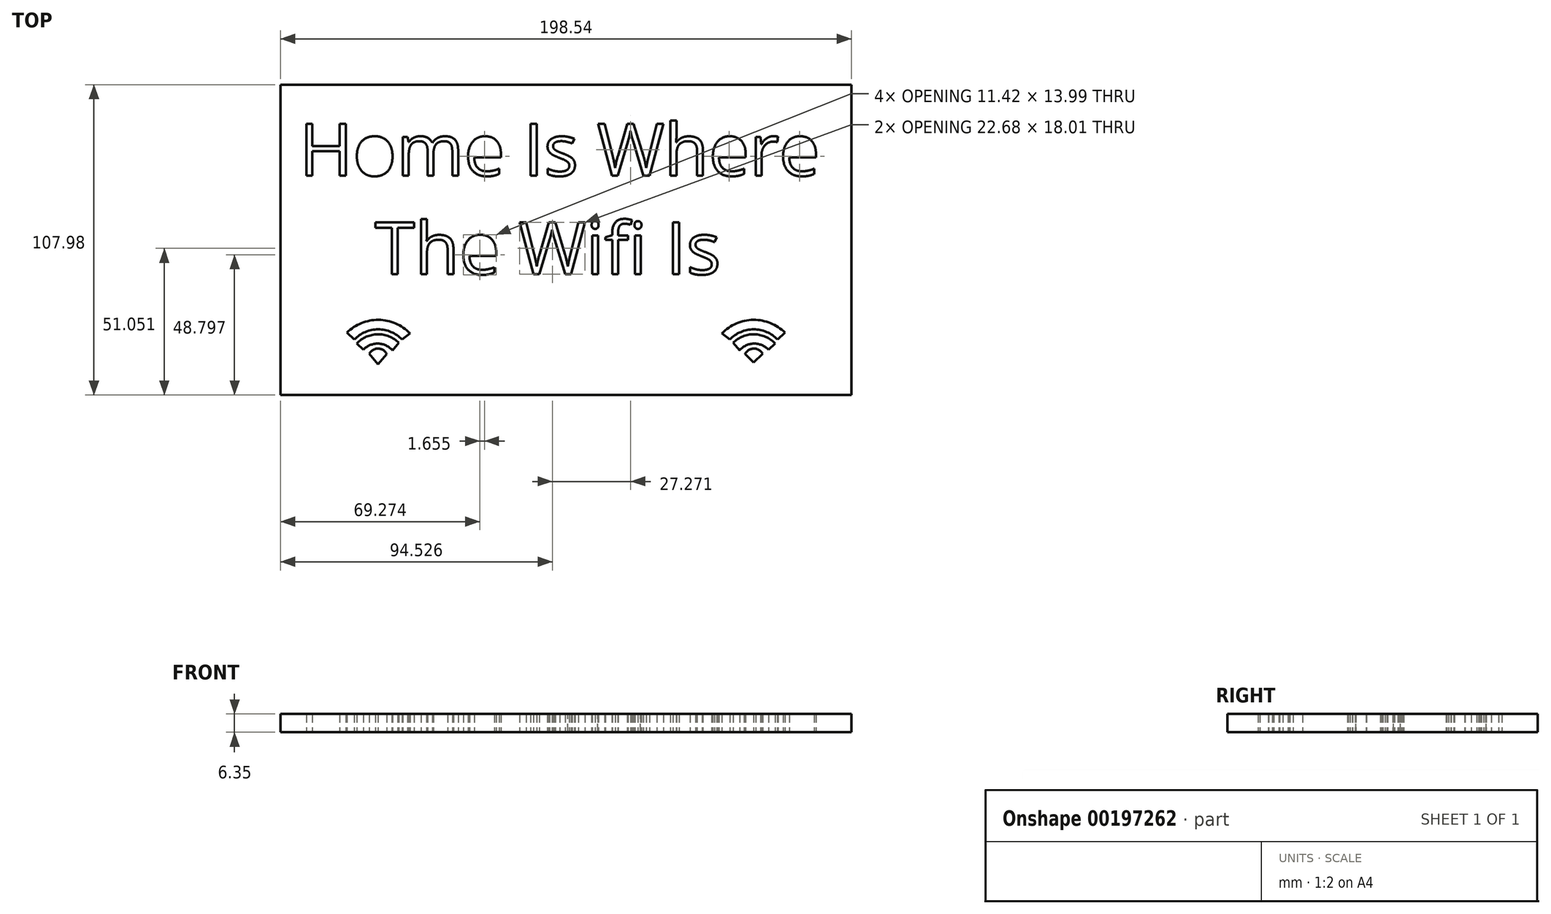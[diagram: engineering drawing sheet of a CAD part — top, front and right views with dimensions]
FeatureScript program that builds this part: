
annotation { "Feature Type Name" : "Feature", "Feature Type Description" : "" }
export const myFeature = defineFeature(function(context is Context, id is Id, definition is map)
    precondition{}
    {
        {
            var Q0;
            Q0=qCreatedBy(makeId("Top.planeOp"),FACE);
            var sketch = newSketch(context, id + "F0", { "sketchPlane" : qUnion([Q0])});
            skText(sketch, "E0", { "text": "Home Is Where \n    The Wifi Is", "fontName": "OpenSans-Regular.ttf"});
            skPoint(sketch, "E1.middle", {"position": v(-127.1, 81.3) * mm});
            skLineSegment(sketch, "E2.bottom", {"start": v(99.27, -53.99) * mm, "end": v(-99.27, -53.99) * mm});
            skLineSegment(sketch, "E2.top", {"start": v(99.27, 53.99) * mm, "end": v(-99.27, 53.99) * mm});
            skLineSegment(sketch, "E2.left", {"start": v(99.27, -53.99) * mm, "end": v(99.27, 53.99) * mm});
            skLineSegment(sketch, "E2.right", {"start": v(-99.27, -53.99) * mm, "end": v(-99.27, 53.99) * mm});
            skPoint(sketch, "E2.middle", {"position": v(0, 0) * mm});
            skLineSegment(sketch, "E3", {"start": v(0, 0) * mm, "end": v(0, -53.99) * mm});
            skArc(sketch, "E4", {"start": v(-54.28, -32.5) * mm, "mid": v(-65.2, -27.82) * mm, "end": v(-76.23, -32.28) * mm});
            skArc(sketch, "E5", {"start": v(-57, -34.66) * mm, "mid": v(-65.31, -31.12) * mm, "end": v(-73.63, -34.66) * mm});
            skArc(sketch, "E6", {"start": v(-58.12, -35.79) * mm, "mid": v(-65.47, -32.83) * mm, "end": v(-72.72, -36.01) * mm});
            skArc(sketch, "E7", {"start": v(-60.39, -38.4) * mm, "mid": v(-65.38, -36.08) * mm, "end": v(-70.46, -38.16) * mm});
            skArc(sketch, "E8", {"start": v(-62.31, -39.75) * mm, "mid": v(-65.33, -37.8) * mm, "end": v(-68.42, -39.64) * mm});
            skLineSegment(sketch, "E9", {"start": v(-76.23, -32.28) * mm, "end": v(-73.63, -34.66) * mm});
            skLineSegment(sketch, "E10", {"start": v(-54.28, -32.5) * mm, "end": v(-57, -34.66) * mm});
            skLineSegment(sketch, "E11", {"start": v(-72.72, -36.01) * mm, "end": v(-70.46, -38.16) * mm});
            skLineSegment(sketch, "E12", {"start": v(-58.12, -35.79) * mm, "end": v(-60.39, -38.4) * mm});
            skLineSegment(sketch, "E13", {"start": v(-68.42, -39.64) * mm, "end": v(-65.37, -43.3) * mm});
            skArc(sketch, "E14.MirrorCS", {"start": v(54.28, -32.5) * mm, "mid": v(65.2, -27.82) * mm, "end": v(76.23, -32.28) * mm});
            skLineSegment(sketch, "E15.MirrorCS", {"start": v(76.23, -32.28) * mm, "end": v(73.63, -34.66) * mm});
            skLineSegment(sketch, "E16.MirrorCS", {"start": v(54.28, -32.5) * mm, "end": v(57, -34.66) * mm});
            skArc(sketch, "E17.MirrorCS", {"start": v(57, -34.66) * mm, "mid": v(65.31, -31.12) * mm, "end": v(73.63, -34.66) * mm});
            skArc(sketch, "E18.MirrorCS", {"start": v(58.12, -35.79) * mm, "mid": v(65.47, -32.83) * mm, "end": v(72.72, -36.01) * mm});
            skLineSegment(sketch, "E19.MirrorCS", {"start": v(72.72, -36.01) * mm, "end": v(70.46, -38.16) * mm});
            skLineSegment(sketch, "E20.MirrorCS", {"start": v(58.12, -35.79) * mm, "end": v(60.39, -38.4) * mm});
            skArc(sketch, "E21.MirrorCS", {"start": v(60.39, -38.4) * mm, "mid": v(65.38, -36.08) * mm, "end": v(70.46, -38.16) * mm});
            skArc(sketch, "E22.MirrorCS", {"start": v(62.31, -39.75) * mm, "mid": v(65.33, -37.8) * mm, "end": v(68.42, -39.64) * mm});
            skLineSegment(sketch, "E23.MirrorCS", {"start": v(62.31, -39.75) * mm, "end": v(65.31, -42.69) * mm});
            skLineSegment(sketch, "E24", {"start": v(-62.31, -39.75) * mm, "end": v(-65.37, -43.3) * mm});
            skLineSegment(sketch, "E25", {"start": v(68.42, -39.64) * mm, "end": v(65.31, -42.69) * mm});
            const initialGuessF0  = {"E0": [-0.09277, 0.02236, 1, 0, 0.01816]};
            skSetInitialGuess(sketch, initialGuessF0);
            skSolve(sketch);
        }
        {
            var Q0;
            Q0=makeQuery(id+"F0.imprint","IMPRINT",FACE,{"disambiguationData":[TD([[makeQuery(id+"F0.imprint","IMPRINT",EDGE,{"derivedFrom":sQuery(id+"F0.wireOp",EDGE,"E0.sketch_text.stroke-0")}),1.0]])]});
            extrude(context, id + "F1", {"entities" : qUnion([Q0]), "depth" : 6.35 * mm});
        }
    });
